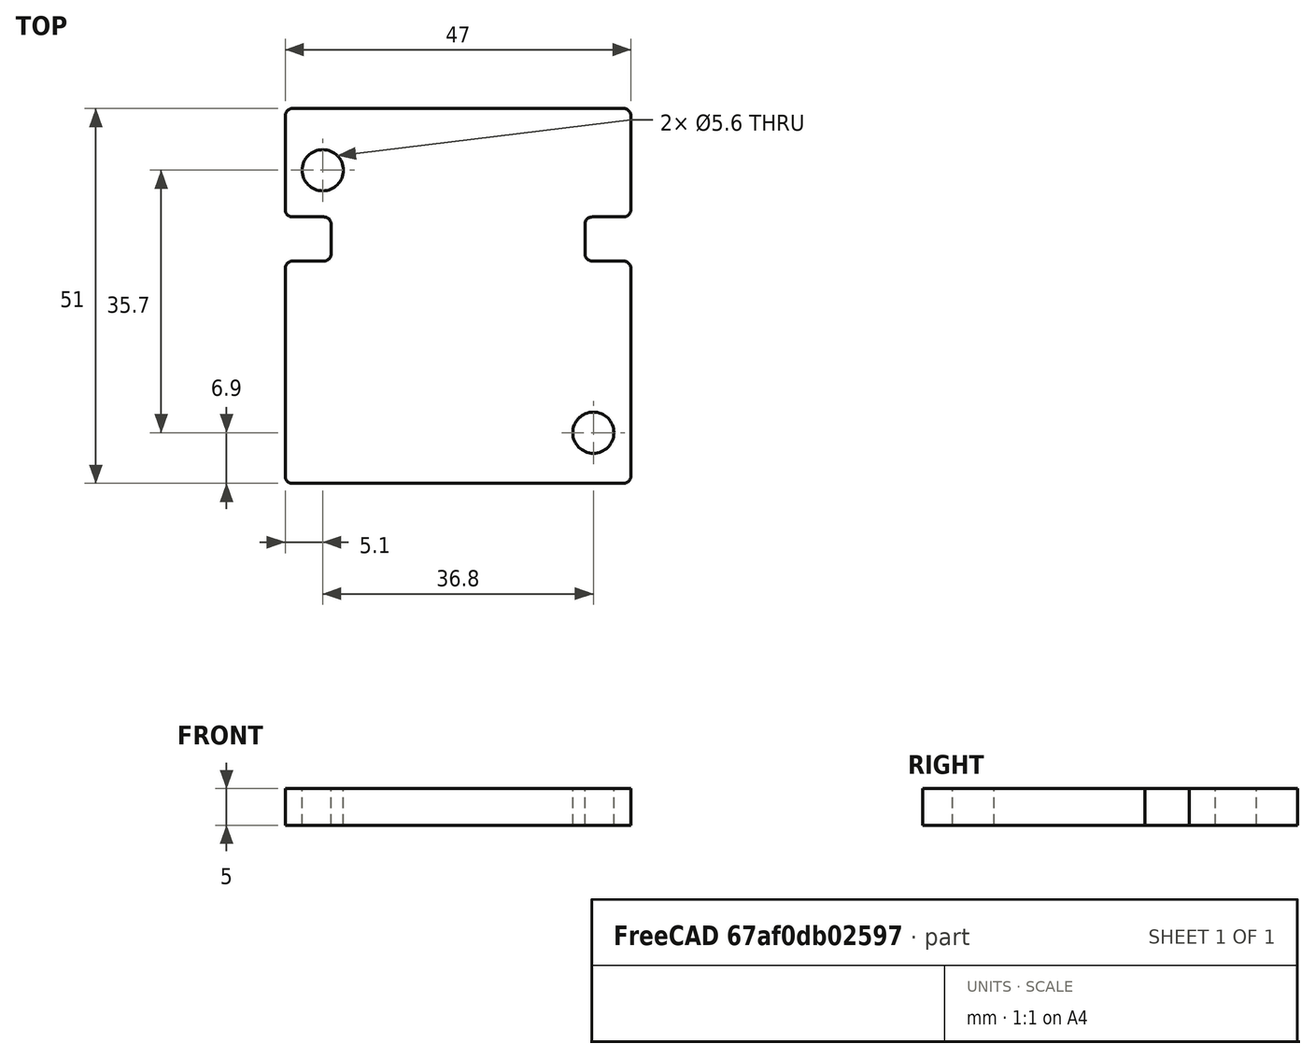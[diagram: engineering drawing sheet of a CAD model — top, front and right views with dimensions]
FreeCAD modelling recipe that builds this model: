
FCSTD DOCUMENT  (FreeCAD 0.19R24276 (Git))
Label: Mounting Plate
License: All rights reserved
LicenseURL: http://en.wikipedia.org/wiki/All_rights_reserved
objects: Part::Box×3, Part::Cut×3, Part::Fillet×3, Part::Cylinder×2, Part::MultiFuse×1
note: 12 computed .brp shape members not serialized (recipe doc carries the construction recipe); baked Part::Feature solids carry a one-line shape summary decoded from their .brp

FEATURE [Part::Box] Box  label="Cube"
  AttacherType = Attacher::AttachEngine3D
  Height = 5
  Length = 47
  Width = 51
FEATURE [Part::Cylinder] Cylinder
  Angle = 360
  AttacherType = Attacher::AttachEngine3D
  Height = 10
  Placement = pos=(5.1,42.6,-2) rot=(0,0,1;0rad)
  Radius = 2.8
FEATURE [Part::Cut] Cut
  Base = -> Box
  Tool = -> Cylinder
FEATURE [Part::Cylinder] Cylinder001
  Angle = 360
  AttacherType = Attacher::AttachEngine3D
  Height = 10
  Placement = pos=(41.9,6.9,-2) rot=(0,0,1;0rad)
  Radius = 2.8
FEATURE [Part::Cut] Cut001
  Base = -> Cut
  Tool = -> Cylinder001
FEATURE [Part::Box] Box001  label="Cube001"
  AttacherType = Attacher::AttachEngine3D
  Height = 10
  Length = 6.25
  Placement = pos=(0,30.25,-2) rot=(0,0,1;0rad)
  Width = 6
FEATURE [Part::Box] Box002  label="Cube002"
  AttacherType = Attacher::AttachEngine3D
  Height = 10
  Length = 6.25
  Placement = pos=(40.75,30.25,-2) rot=(0,0,1;0rad)
  Width = 6
FEATURE [Part::MultiFuse] Fusion
  Shapes = -> [Box001,Box002]
FEATURE [Part::Cut] Cut002
  Base = -> Cut001
  Tool = -> Fusion
FEATURE [Part::Fillet] Fillet
  Base = -> Cut002
  Edges = 4 edges r=1: [Edge4,Edge32,Edge35,Edge36]
FEATURE [Part::Fillet] Fillet001
  Base = -> Fillet
  Edges = 4 edges r=1: [Edge4,Edge44,Edge45,Edge51]
FEATURE [Part::Fillet] Fillet002  label="Oringal Plate design 0.2"
  Base = -> Fillet001
  Edges = 4 edges r=1: [Edge49,Edge51,Edge58,Edge60]
